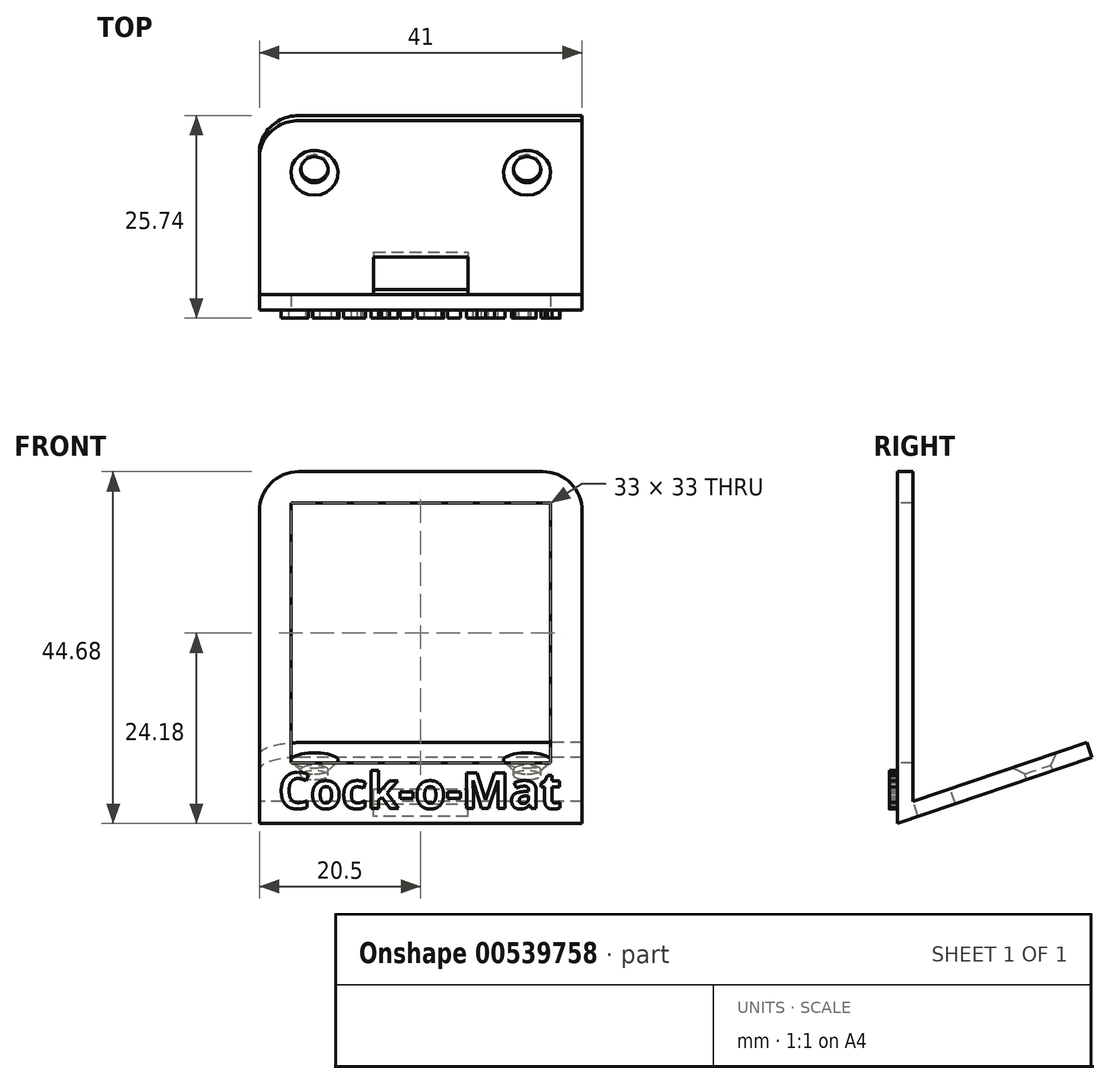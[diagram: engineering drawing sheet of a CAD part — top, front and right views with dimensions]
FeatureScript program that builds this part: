
annotation { "Feature Type Name" : "Feature", "Feature Type Description" : "" }
export const myFeature = defineFeature(function(context is Context, id is Id, definition is map)
    precondition{}
    {
        {
            var Q0;
            Q0=qCreatedBy(makeId("Front.planeOp"),FACE);
            var sketch = newSketch(context, id + "F0", { "sketchPlane" : qUnion([Q0])});
            skLineSegment(sketch, "E0.bottom", {"start": v(2, 2) * mm, "end": v(43, 2) * mm});
            skLineSegment(sketch, "E0.top", {"start": v(2, 46) * mm, "end": v(43, 46) * mm});
            skLineSegment(sketch, "E0.left", {"start": v(2, 2) * mm, "end": v(2, 46) * mm});
            skLineSegment(sketch, "E0.right", {"start": v(43, 2) * mm, "end": v(43, 46) * mm});
            skLineSegment(sketch, "E1.bottom", {"start": v(0, 0) * mm, "end": v(45, 0) * mm});
            skLineSegment(sketch, "E1.top", {"start": v(0, 48) * mm, "end": v(45, 48) * mm});
            skLineSegment(sketch, "E1.left", {"start": v(0, 0) * mm, "end": v(0, 48) * mm});
            skLineSegment(sketch, "E1.right", {"start": v(45, 0) * mm, "end": v(45, 48) * mm});
            skLineSegment(sketch, "E2.bottom", {"start": v(6, 9) * mm, "end": v(39, 9) * mm});
            skLineSegment(sketch, "E2.top", {"start": v(6, 42) * mm, "end": v(39, 42) * mm});
            skLineSegment(sketch, "E2.left", {"start": v(6, 9) * mm, "end": v(6, 42) * mm});
            skLineSegment(sketch, "E2.right", {"start": v(39, 9) * mm, "end": v(39, 42) * mm});
            skText(sketch, "E3", { "text": "Cock-o-Mat", "fontName": "OpenSans-Bold.ttf"});
            skPoint(sketch, "E4", {"position": v(22.5, 2) * mm});
            const initialGuessF0  = {"E3": [0.0044, 0.0032, 1, 0, 0.0046]};
            skSetInitialGuess(sketch, initialGuessF0);
            skSolve(sketch);
        }
        {
            var Q0;
            Q0=makeQuery(id+"F0.imprint","IMPRINT",FACE,{"disambiguationData":[TD([[makeQuery(id+"F0.imprint","IMPRINT",EDGE,{"derivedFrom":sQuery(id+"F0.wireOp",EDGE,"E3.sketch_text.stroke-132")}),-1.0]])]});
            var Q1;
            Q1=makeQuery(id+"F0.imprint","IMPRINT",FACE,{"disambiguationData":[TD([[makeQuery(id+"F0.imprint","IMPRINT",EDGE,{"derivedFrom":sQuery(id+"F0.wireOp",EDGE,"E3.sketch_text.stroke-15")}),-1.0]])]});
            var Q2;
            Q2=makeQuery(id+"F0.imprint","IMPRINT",FACE,{"disambiguationData":[TD([[makeQuery(id+"F0.imprint","IMPRINT",EDGE,{"derivedFrom":sQuery(id+"F0.wireOp",EDGE,"E3.sketch_text.stroke-88")}),-1.0]])]});
            var Q3;
            Q3=makeQuery(id+"F0.imprint","IMPRINT",FACE,{"disambiguationData":[TD([[makeQuery(id+"F0.imprint","IMPRINT",EDGE,{"derivedFrom":sQuery(id+"F0.wireOp",EDGE,"E3.sketch_text.stroke-66")}),-1.0]])]});
            var Q4;
            Q4=makeQuery(id+"F0.imprint","IMPRINT",FACE,{"disambiguationData":[TD([[makeQuery(id+"F0.imprint","IMPRINT",EDGE,{"derivedFrom":sQuery(id+"F0.wireOp",EDGE,"E3.sketch_text.stroke-47")}),-1.0]])]});
            var Q5;
            Q5=makeQuery(id+"F0.imprint","IMPRINT",FACE,{"disambiguationData":[TD([[makeQuery(id+"F0.imprint","IMPRINT",EDGE,{"derivedFrom":sQuery(id+"F0.wireOp",EDGE,"E0.bottom")}),1.0]])]});
            var Q6;
            Q6=makeQuery(id+"F0.imprint","IMPRINT",FACE,{"disambiguationData":[TD([[makeQuery(id+"F0.imprint","IMPRINT",EDGE,{"derivedFrom":sQuery(id+"F0.wireOp",EDGE,"E3.sketch_text.stroke-0")}),-1.0]])]});
            var Q7;
            Q7=makeQuery(id+"F0.imprint","IMPRINT",FACE,{"disambiguationData":[TD([[makeQuery(id+"F0.imprint","IMPRINT",EDGE,{"derivedFrom":sQuery(id+"F0.wireOp",EDGE,"E3.sketch_text.stroke-107")}),-1.0]])]});
            var Q8;
            Q8=makeQuery(id+"F0.imprint","IMPRINT",FACE,{"disambiguationData":[TD([[makeQuery(id+"F0.imprint","IMPRINT",EDGE,{"derivedFrom":sQuery(id+"F0.wireOp",EDGE,"E3.sketch_text.stroke-33")}),-1.0]])]});
            var Q9;
            Q9=makeQuery(id+"F0.imprint","IMPRINT",FACE,{"disambiguationData":[TD([[makeQuery(id+"F0.imprint","IMPRINT",EDGE,{"derivedFrom":sQuery(id+"F0.wireOp",EDGE,"E3.sketch_text.stroke-15")}),1.0]])]});
            var Q10;
            Q10=makeQuery(id+"F0.imprint","IMPRINT",FACE,{"disambiguationData":[TD([[makeQuery(id+"F0.imprint","IMPRINT",EDGE,{"derivedFrom":sQuery(id+"F0.wireOp",EDGE,"E3.sketch_text.stroke-66")}),1.0]])]});
            var Q11;
            Q11=makeQuery(id+"F0.imprint","IMPRINT",FACE,{"disambiguationData":[TD([[makeQuery(id+"F0.imprint","IMPRINT",EDGE,{"derivedFrom":sQuery(id+"F0.wireOp",EDGE,"E3.sketch_text.stroke-125")}),1.0]])]});
            var Q12;
            Q12=makeQuery(id+"F0.imprint","IMPRINT",FACE,{"disambiguationData":[TD([[makeQuery(id+"F0.imprint","IMPRINT",EDGE,{"derivedFrom":sQuery(id+"F0.wireOp",EDGE,"E3.sketch_text.stroke-62")}),-1.0]])]});
            var Q13;
            Q13=makeQuery(id+"F0.imprint","IMPRINT",FACE,{"disambiguationData":[TD([[makeQuery(id+"F0.imprint","IMPRINT",EDGE,{"derivedFrom":sQuery(id+"F0.wireOp",EDGE,"E3.sketch_text.stroke-84")}),-1.0]])]});
            extrude(context, id + "F1", {"entities" : qUnion([Q0, Q1, Q2, Q3, Q4, Q5, Q6, Q7, Q8, Q9, Q10, Q11, Q12, Q13]), "oppositeDirection" : true, "depth" : 2 * mm, "offsetDistance" : 25 * mm});
        }
        {
            var Q0;
            Q0=makeQuery(id+"F1.opExtrude","SWEPT_FACE",FACE,{"disambiguationData":[OSD([sQuery(id+"F0.wireOp",EDGE,"E0.left")])]});
            var sketch = newSketch(context, id + "F2", { "sketchPlane" : qUnion([Q0])});
            skLineSegment(sketch, "E5", {"start": v(-2, 2) * mm, "end": v(-24.74, 9.68) * mm});
            skLineSegment(sketch, "E6", {"start": v(-24.74, 9.68) * mm, "end": v(-24.1, 11.58) * mm});
            skLineSegment(sketch, "E7", {"start": v(-24.1, 11.58) * mm, "end": v(-2, 4.11) * mm});
            skLineSegment(sketch, "E8", {"start": v(-2, 2) * mm, "end": v(0, 1.32) * mm});
            skLineSegment(sketch, "E9", {"start": v(0, 1.32) * mm, "end": v(0, 2) * mm});
            skSolve(sketch);
        }
        {
            var Q0;
            {var subQ0=sQuery(id+"F2.wireOp",EDGE,"E5");Q0=makeQuery(id+"F2.imprint","IMPRINT",FACE,{"disambiguationData":[TD([[makeQuery(id+"F2.imprint","IMPRINT",EDGE,{"derivedFrom":subQ0}),-1.0]])]});}
            var Q1;
            Q1=makeQuery(id+"F2.imprint","IMPRINT",FACE,{"disambiguationData":[TD([[makeQuery(id+"F2.imprint","IMPRINT",EDGE,{"derivedFrom":sQuery(id+"F2.wireOp",EDGE,"E8")}),1.0]])]});
            var Q2;
            Q2=makeQuery(id+"F1.opExtrude","SWEPT_FACE",FACE,{"disambiguationData":[OSD([sQuery(id+"F0.wireOp",EDGE,"E0.right")])]});
            extrude(context, id + "F3", {"entities" : qUnion([Q0, Q1]), "operationType" : NewBodyOperationType.ADD, "endBound" : BoundingType.UP_TO_SURFACE, "oppositeDirection" : true, "depth" : 25 * mm, "endBoundEntityFace" : qUnion([Q2]), "offsetDistance" : 25 * mm});
        }
        {
            var Q0;
            Q0=makeQuery(id+"F3.opExtrude","SWEPT_FACE",FACE,{"disambiguationData":[OSD([sQuery(id+"F2.wireOp",EDGE,"E7")])]});
            var sketch = newSketch(context, id + "F4", { "sketchPlane" : qUnion([Q0])});
            skPoint(sketch, "E10", {"position": v(36, 19.53) * mm});
            skLineSegment(sketch, "E11", {"start": v(22.5, 26.53) * mm, "end": v(22.5, -9.9) * mm, "construction": true});
            skPoint(sketch, "E12.MirrorP", {"position": v(9, 19.53) * mm});
            skLineSegment(sketch, "E13.bottom", {"start": v(16.5, 3.21) * mm, "end": v(28.5, 3.21) * mm});
            skLineSegment(sketch, "E13.top", {"start": v(16.5, 8.21) * mm, "end": v(28.5, 8.21) * mm});
            skLineSegment(sketch, "E13.left", {"start": v(16.5, 3.21) * mm, "end": v(16.5, 8.21) * mm});
            skLineSegment(sketch, "E13.right", {"start": v(28.5, 3.21) * mm, "end": v(28.5, 8.21) * mm});
            skSolve(sketch);
        }
        {
            var Q0;
            Q0=sQuery(id+"F4.wireOp",VERTEX,"E10");
            var Q1;
            Q1=sQuery(id+"F4.wireOp",VERTEX,"E12.MirrorP");
            var Q2;
            Q2=makeQuery(id+"F1.opExtrude","SWEPT_BODY",BODY,{"disambiguationData":[OSD([sQuery(id+"F0.wireOp",EDGE,"dBrt7hmd-mTI9-i96z-zq7e-3Vyq4qFtwWi6"),sQuery(id+"F0.wireOp",EDGE,"3f478bf5-4f6b-4b60-86fd-c730006928be.1.0.0"),sQuery(id+"F0.wireOp",EDGE,"3f478bf5-4f6b-4b60-86fd-c730006928be.2.0.0"),sQuery(id+"F0.wireOp",EDGE,"3f478bf5-4f6b-4b60-86fd-c730006928be.3.0.0"),sQuery(id+"F0.wireOp",EDGE,"E0.bottom"),sQuery(id+"F0.wireOp",EDGE,"E0.top"),sQuery(id+"F0.wireOp",EDGE,"E0.left"),sQuery(id+"F0.wireOp",EDGE,"E0.right")])]});
            hole(context, id + "F5", {"style" : HoleStyle.C_SINK, "endStyle" : HoleEndStyle.THROUGH, "holeDiameter" : 3.5 * mm, "cSinkDiameter" : 6 * mm, "cSinkAngle" : 90 * degree, "majorDiameter" : 5 * mm, "isTappedThrough" : true, "tappedDepth" : 12 * mm, "tapClearance" : 3, "locations" : qUnion([Q0, Q1]), "scope" : qUnion([Q2])});
        }
        {
            var Q0;
            Q0=makeQuery(id+"F1.opExtrude","SWEPT_EDGE",EDGE,{"disambiguationData":[OSD([sQuery(id+"F0.wireOp",EDGE,"E0.top"),sQuery(id+"F0.wireOp",EDGE,"E0.left")])]});
            var Q1;
            Q1=makeQuery(id+"F1.opExtrude","SWEPT_EDGE",EDGE,{"disambiguationData":[OSD([sQuery(id+"F0.wireOp",EDGE,"E0.top"),sQuery(id+"F0.wireOp",EDGE,"E0.right")])]});
            var Q2;
            Q2=makeQuery(id+"F3.opExtrude","CAP_EDGE",EDGE,{"disambiguationData":[OSD([sQuery(id+"F2.wireOp",EDGE,"E6")])],"isStart":true});
            var Q3;
            Q3=makeQuery(id+"F3.opExtrude","TWEAK_EDGE",EDGE,{"derivedFrom":[makeQuery(id+"F1.opExtrude","SWEPT_FACE",FACE,{"disambiguationData":[OSD([sQuery(id+"F0.wireOp",EDGE,"E0.right")])]}),makeQuery(id+"F2.imprint","IMPRINT",EDGE,{"derivedFrom":sQuery(id+"F2.wireOp",EDGE,"E6")})]});
            fillet(context, id + "F6", {"entities" : qUnion([Q0, Q1, Q2, Q3]), "radius" : 5 * mm, "tangentPropagation" : true, "allowEdgeOverflow" : false});
        }
        {
            var Q0;
            Q0=makeQuery(id+"F4.imprint","IMPRINT",FACE,{"disambiguationData":[TD([[makeQuery(id+"F4.imprint","IMPRINT",EDGE,{"derivedFrom":sQuery(id+"F4.wireOp",EDGE,"E13.bottom")}),-1.0]])]});
            extrude(context, id + "F7", {"entities" : qUnion([Q0]), "operationType" : NewBodyOperationType.REMOVE, "endBound" : BoundingType.THROUGH_ALL, "oppositeDirection" : true, "depth" : 25 * mm, "offsetDistance" : 25 * mm});
        }
        {
            var Q0;
            Q0=makeQuery(id+"F0.imprint","IMPRINT",FACE,{"disambiguationData":[TD([[makeQuery(id+"F0.imprint","IMPRINT",EDGE,{"derivedFrom":sQuery(id+"F0.wireOp",EDGE,"E3.sketch_text.stroke-62")}),-1.0]])]});
            var Q1;
            Q1=makeQuery(id+"F0.imprint","IMPRINT",FACE,{"disambiguationData":[TD([[makeQuery(id+"F0.imprint","IMPRINT",EDGE,{"derivedFrom":sQuery(id+"F0.wireOp",EDGE,"E3.sketch_text.stroke-0")}),-1.0]])]});
            var Q2;
            Q2=makeQuery(id+"F0.imprint","IMPRINT",FACE,{"disambiguationData":[TD([[makeQuery(id+"F0.imprint","IMPRINT",EDGE,{"derivedFrom":sQuery(id+"F0.wireOp",EDGE,"E3.sketch_text.stroke-15")}),-1.0]])]});
            var Q3;
            Q3=makeQuery(id+"F0.imprint","IMPRINT",FACE,{"disambiguationData":[TD([[makeQuery(id+"F0.imprint","IMPRINT",EDGE,{"derivedFrom":sQuery(id+"F0.wireOp",EDGE,"E3.sketch_text.stroke-33")}),-1.0]])]});
            var Q4;
            Q4=makeQuery(id+"F0.imprint","IMPRINT",FACE,{"disambiguationData":[TD([[makeQuery(id+"F0.imprint","IMPRINT",EDGE,{"derivedFrom":sQuery(id+"F0.wireOp",EDGE,"E3.sketch_text.stroke-47")}),-1.0]])]});
            var Q5;
            Q5=makeQuery(id+"F0.imprint","IMPRINT",FACE,{"disambiguationData":[TD([[makeQuery(id+"F0.imprint","IMPRINT",EDGE,{"derivedFrom":sQuery(id+"F0.wireOp",EDGE,"E3.sketch_text.stroke-66")}),-1.0]])]});
            var Q6;
            Q6=makeQuery(id+"F0.imprint","IMPRINT",FACE,{"disambiguationData":[TD([[makeQuery(id+"F0.imprint","IMPRINT",EDGE,{"derivedFrom":sQuery(id+"F0.wireOp",EDGE,"E3.sketch_text.stroke-84")}),-1.0]])]});
            var Q7;
            Q7=makeQuery(id+"F0.imprint","IMPRINT",FACE,{"disambiguationData":[TD([[makeQuery(id+"F0.imprint","IMPRINT",EDGE,{"derivedFrom":sQuery(id+"F0.wireOp",EDGE,"E3.sketch_text.stroke-88")}),-1.0]])]});
            var Q8;
            Q8=makeQuery(id+"F0.imprint","IMPRINT",FACE,{"disambiguationData":[TD([[makeQuery(id+"F0.imprint","IMPRINT",EDGE,{"derivedFrom":sQuery(id+"F0.wireOp",EDGE,"E3.sketch_text.stroke-107")}),-1.0]])]});
            var Q9;
            Q9=makeQuery(id+"F0.imprint","IMPRINT",FACE,{"disambiguationData":[TD([[makeQuery(id+"F0.imprint","IMPRINT",EDGE,{"derivedFrom":sQuery(id+"F0.wireOp",EDGE,"E3.sketch_text.stroke-132")}),-1.0]])]});
            extrude(context, id + "F8", {"entities" : qUnion([Q0, Q1, Q2, Q3, Q4, Q5, Q6, Q7, Q8, Q9]), "operationType" : NewBodyOperationType.ADD, "depth" : 1 * mm, "offsetDistance" : 25 * mm});
        }
    });
